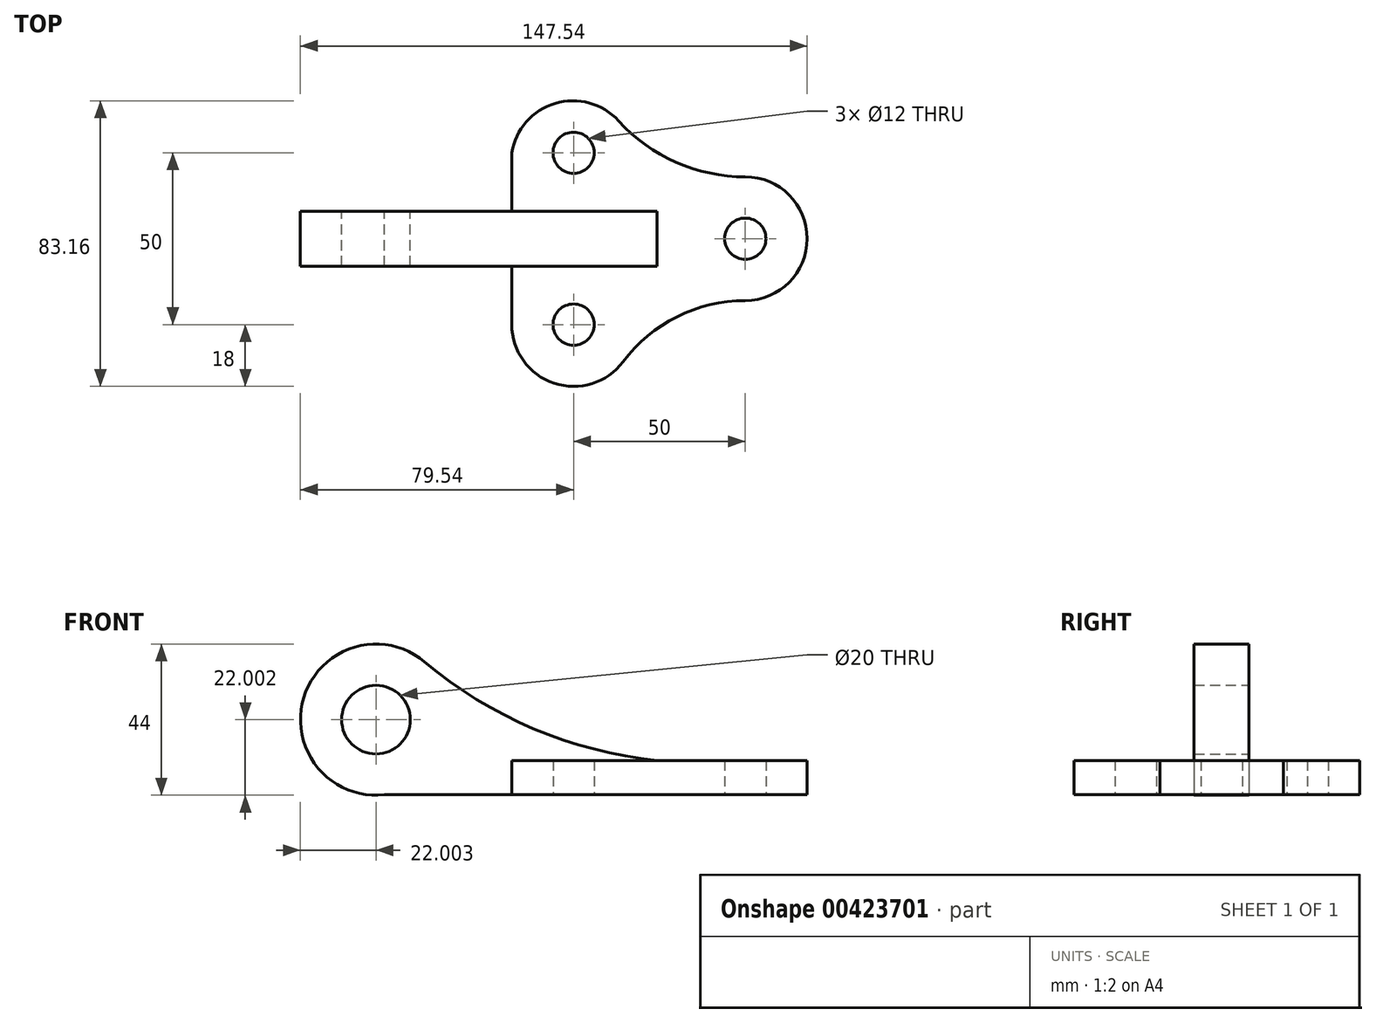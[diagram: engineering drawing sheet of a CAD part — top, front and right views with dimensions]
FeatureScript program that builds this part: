
annotation { "Feature Type Name" : "Feature", "Feature Type Description" : "" }
export const myFeature = defineFeature(function(context is Context, id is Id, definition is map)
    precondition{}
    {
        {
            var Q0;
            Q0=qCreatedBy(makeId("Top.planeOp"),FACE);
            var sketch = newSketch(context, id + "F0", { "sketchPlane" : qUnion([Q0])});
            skCircle(sketch, "E0", {"center": v(0, 0) * mm, "radius": 6 * mm});
            skArc(sketch, "E1", {"start": v(0, -18) * mm, "mid": v(18, 0) * mm, "end": v(0, 18) * mm});
            skCircle(sketch, "E2", {"center": v(-50, 25) * mm, "radius": 6 * mm});
            skCircle(sketch, "E3", {"center": v(-50, -25) * mm, "radius": 6 * mm});
            skArc(sketch, "E4", {"start": v(-36.93, 34.3) * mm, "mid": v(-55.38, 39.4) * mm, "end": v(-68, 25) * mm});
            skArc(sketch, "E5", {"start": v(-68, -25) * mm, "mid": v(-55.7, -42.08) * mm, "end": v(-35.6, -35.8) * mm});
            skArc(sketch, "E6", {"start": v(-36.93, 34.3) * mm, "mid": v(-20.18, 22.25) * mm, "end": v(0, 18) * mm});
            skArc(sketch, "E7", {"start": v(0, -18) * mm, "mid": v(-19.9, -22.7) * mm, "end": v(-35.6, -35.8) * mm});
            skLineSegment(sketch, "E8", {"start": v(-68, 25) * mm, "end": v(-68, -25) * mm});
            skSolve(sketch);
        }
        {
            var Q0;
            Q0=makeQuery(id+"F0.imprint","IMPRINT",FACE,{"disambiguationData":[TD([[makeQuery(id+"F0.imprint","IMPRINT",EDGE,{"derivedFrom":sQuery(id+"F0.wireOp",EDGE,"E0")}),-1.0]])]});
            extrude(context, id + "F1", {"entities" : qUnion([Q0]), "depth" : 10 * mm});
        }
        {
            var Q0;
            Q0=qCreatedBy(makeId("Front.planeOp"),FACE);
            var sketch = newSketch(context, id + "F2", { "sketchPlane" : qUnion([Q0])});
            skLineSegment(sketch, "E9", {"start": v(-6, 0) * mm, "end": v(-6, 10) * mm});
            skLineSegment(sketch, "E10", {"start": v(0, 0) * mm, "end": v(-110, 0) * mm});
            skArc(sketch, "E11", {"start": v(-93.37, 38.7) * mm, "mid": v(-128.6, 28.23) * mm, "end": v(-105.07, 0) * mm});
            skCircle(sketch, "E12", {"center": v(-107.54, 21.86) * mm, "radius": 10 * mm});
            skLineSegment(sketch, "E13.0.0", {"start": v(-36.93, 10) * mm, "end": v(-68, 10) * mm});
            skLineSegment(sketch, "E13.0.2", {"start": v(-68, 10) * mm, "end": v(-35.6, 10) * mm});
            skLineSegment(sketch, "E13.0.3", {"start": v(-35.6, 10) * mm, "end": v(0, 10) * mm});
            skLineSegment(sketch, "E13.0.4", {"start": v(0, 10) * mm, "end": v(18, 10) * mm});
            skLineSegment(sketch, "E13.0.5", {"start": v(0, 10) * mm, "end": v(-36.93, 10) * mm});
            skArc(sketch, "E14", {"start": v(-93.37, 38.7) * mm, "mid": v(-49.6, 14.85) * mm, "end": v(0, 10) * mm});
            skSolve(sketch);
        }
        {
            var Q0;
            Q0 = qSketchRegion(id + "F2", true);
            extrude(context, id + "F3", {"entities" : qUnion([Q0]), "operationType" : NewBodyOperationType.ADD, "depth" : 8 * mm, "hasSecondDirection" : true, "secondDirectionOppositeDirection" : true, "secondDirectionDepth" : 8 * mm});
        }
        {
            var Q0;
            Q0=makeQuery(id+"F3.boolean.opBoolean","MERGE",FACE,{"derivedFrom":[makeQuery(id+"F1.opExtrude","CAP_FACE",FACE,{"disambiguationData":[OSD([sQuery(id+"F0.wireOp",EDGE,"E0"),sQuery(id+"F0.wireOp",EDGE,"E1"),sQuery(id+"F0.wireOp",EDGE,"E2"),sQuery(id+"F0.wireOp",EDGE,"E3"),sQuery(id+"F0.wireOp",EDGE,"E4"),sQuery(id+"F0.wireOp",EDGE,"E5"),sQuery(id+"F0.wireOp",EDGE,"E6"),sQuery(id+"F0.wireOp",EDGE,"E7"),sQuery(id+"F0.wireOp",EDGE,"E8")])],"isStart":true}),makeQuery(id+"F3.opExtrude","SWEPT_FACE",FACE,{"disambiguationData":[OSD([sQuery(id+"F2.wireOp",EDGE,"E10")])]})]});
            var sketch = newSketch(context, id + "F4", { "sketchPlane" : qUnion([Q0])});
            skCircle(sketch, "E15.0", {"center": v(0, 0) * mm, "radius": 6 * mm});
            skSolve(sketch);
        }
        {
            var Q0;
            Q0 = qSketchRegion(id + "F4", true);
            extrude(context, id + "F5", {"entities" : qUnion([Q0]), "operationType" : NewBodyOperationType.REMOVE, "oppositeDirection" : true, "depth" : 25 * mm});
        }
    });
